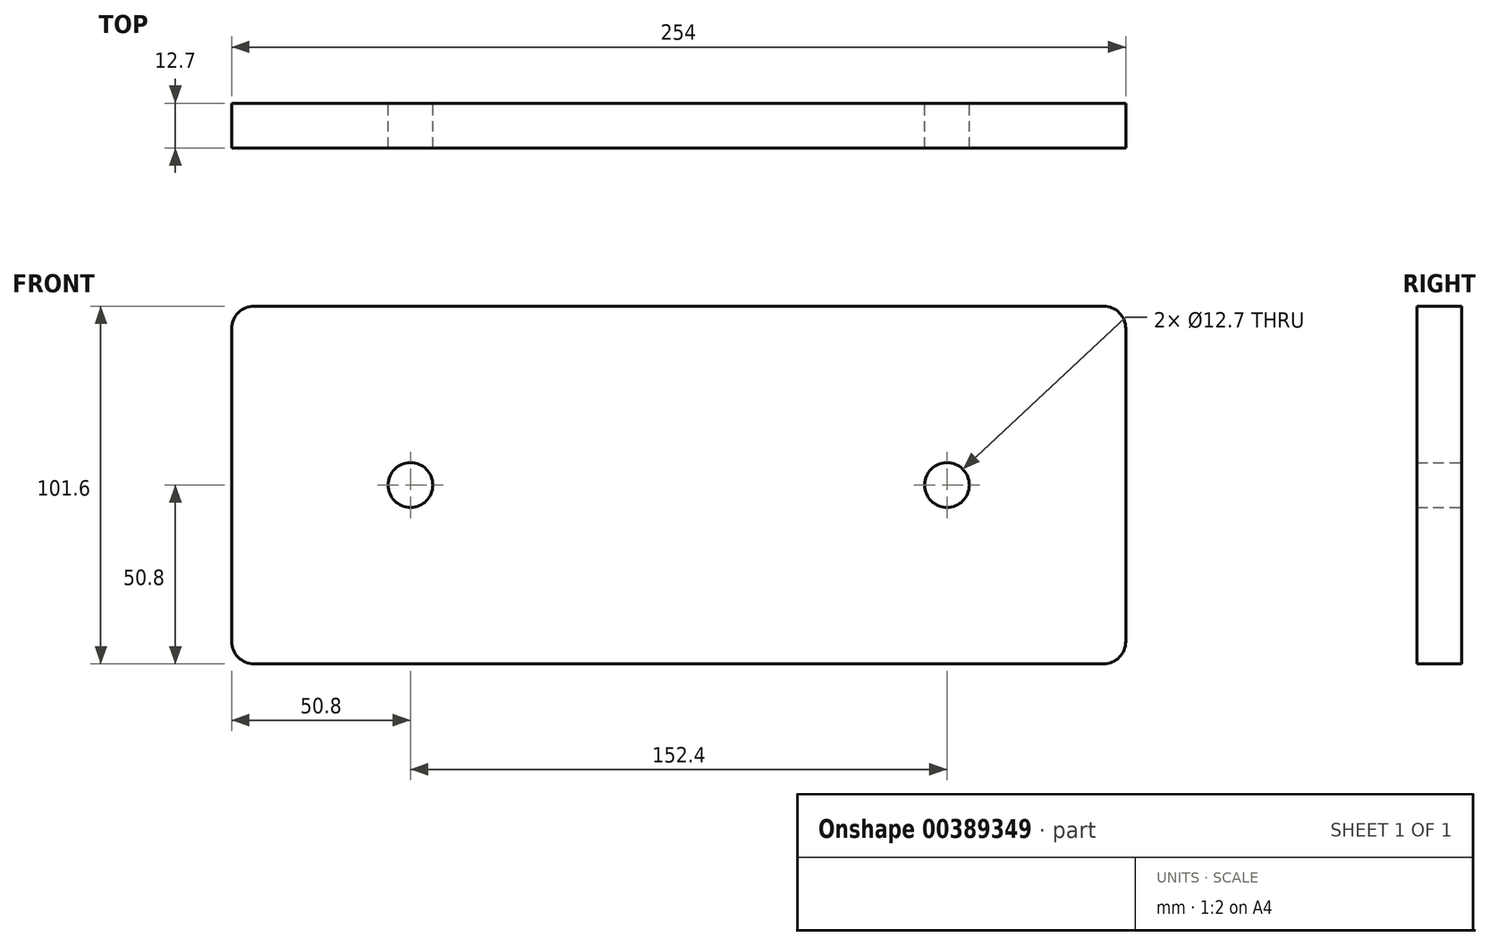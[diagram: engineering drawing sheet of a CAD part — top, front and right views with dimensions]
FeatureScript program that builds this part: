
annotation { "Feature Type Name" : "Feature", "Feature Type Description" : "" }
export const myFeature = defineFeature(function(context is Context, id is Id, definition is map)
    precondition{}
    {
        {
            var Q0;
            Q0=qCreatedBy(makeId("Front.planeOp"),FACE);
            var sketch = newSketch(context, id + "F0", { "sketchPlane" : qUnion([Q0])});
            skLineSegment(sketch, "E0.bottom", {"start": v(0, 0) * mm, "end": v(254, 0) * mm});
            skLineSegment(sketch, "E0.top", {"start": v(0, 101.6) * mm, "end": v(254, 101.6) * mm});
            skLineSegment(sketch, "E0.left", {"start": v(0, 0) * mm, "end": v(0, 101.6) * mm});
            skLineSegment(sketch, "E0.right", {"start": v(254, 0) * mm, "end": v(254, 101.6) * mm});
            skPoint(sketch, "E1", {"position": v(50.8, 50.8) * mm});
            skPoint(sketch, "E2", {"position": v(203.2, 50.8) * mm});
            skSolve(sketch);
        }
        {
            var Q0;
            Q0 = qSketchRegion(id + "F0", true);
            extrude(context, id + "F1", {"entities" : qUnion([Q0]), "depth" : 12.7 * mm});
        }
        {
            var Q0;
            Q0=sQuery(id+"F0.wireOp",VERTEX,"E1");
            var Q1;
            Q1=sQuery(id+"F0.wireOp",VERTEX,"E2");
            var Q2;
            Q2=makeQuery(id+"F1.opExtrude","SWEPT_BODY",BODY,{"disambiguationData":[OSD([sQuery(id+"F0.wireOp",EDGE,"E0.bottom"),sQuery(id+"F0.wireOp",EDGE,"E0.top"),sQuery(id+"F0.wireOp",EDGE,"E0.left"),sQuery(id+"F0.wireOp",EDGE,"E0.right")])]});
            hole(context, id + "F2", {"style" : HoleStyle.SIMPLE, "endStyle" : HoleEndStyle.THROUGH, "oppositeDirection" : true, "holeDiameter" : 12.7 * mm, "isTappedThrough" : true, "tappedDepth" : 12.7 * mm, "tapClearance" : 6, "locations" : qUnion([Q0, Q1]), "scope" : qUnion([Q2])});
        }
        {
            var Q0;
            Q0=makeQuery(id+"F1.opExtrude","SWEPT_EDGE",EDGE,{"disambiguationData":[OSD([sQuery(id+"F0.wireOp",EDGE,"E0.top"),sQuery(id+"F0.wireOp",EDGE,"E0.left")])]});
            var Q1;
            Q1=makeQuery(id+"F1.opExtrude","SWEPT_EDGE",EDGE,{"disambiguationData":[OSD([sQuery(id+"F0.wireOp",EDGE,"E0.bottom"),sQuery(id+"F0.wireOp",EDGE,"E0.left")])]});
            var Q2;
            Q2=makeQuery(id+"F1.opExtrude","SWEPT_EDGE",EDGE,{"disambiguationData":[OSD([sQuery(id+"F0.wireOp",EDGE,"E0.bottom"),sQuery(id+"F0.wireOp",EDGE,"E0.right")])]});
            var Q3;
            Q3=makeQuery(id+"F1.opExtrude","SWEPT_EDGE",EDGE,{"disambiguationData":[OSD([sQuery(id+"F0.wireOp",EDGE,"E0.top"),sQuery(id+"F0.wireOp",EDGE,"E0.right")])]});
            fillet(context, id + "F3", {"entities" : qUnion([Q0, Q1, Q2, Q3]), "radius" : 6.35 * mm, "tangentPropagation" : true, "allowEdgeOverflow" : false});
        }
    });
